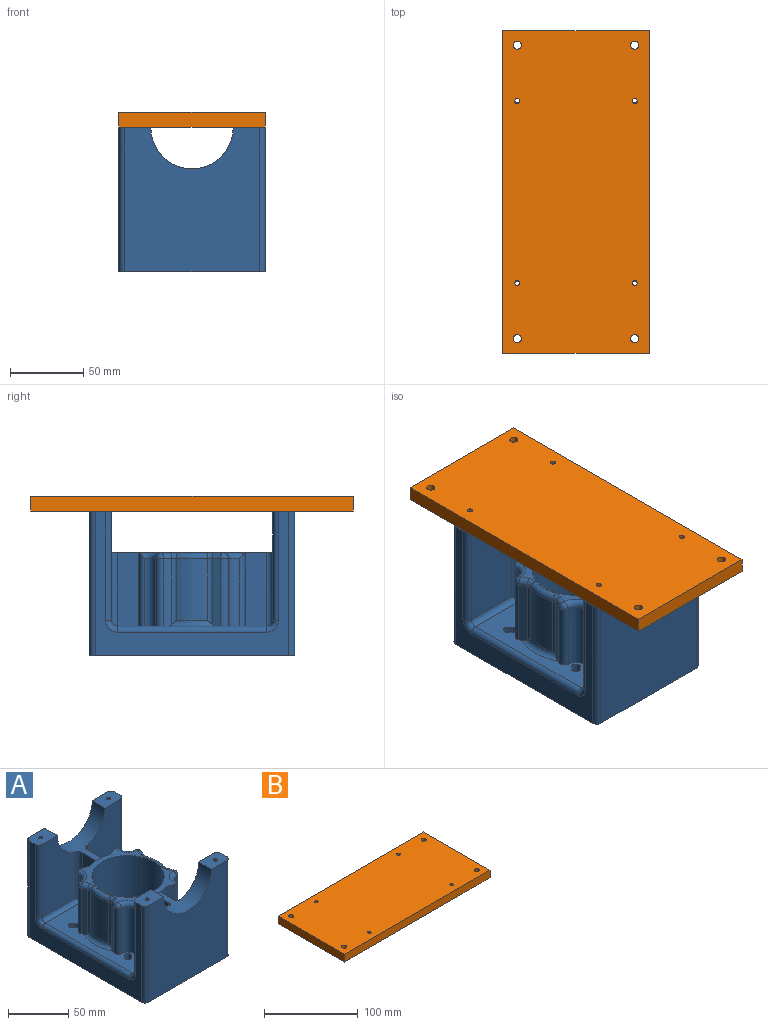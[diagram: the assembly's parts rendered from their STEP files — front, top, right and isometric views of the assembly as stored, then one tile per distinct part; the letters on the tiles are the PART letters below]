
ASSEMBLY  parts=2 mates=1
PART A: 127 faces, bbox 100.1x140.1x98.1 mm
  f0: plane 22x15mm, normal (0,0,1), area 313.5mm2, adj f8,f18,f19,f55,f71,f114,f121
  f1: plane 22x15mm, normal (0,0,1), area 313.5mm2, adj f5,f19,f20,f60,f65,f115,f122
  f2: plane 3x0.16mm, normal (0,-1,0), area 0.2mm2, adj f11,f53,f121
  f3: plane 3x0.16mm, normal (0,1,0), area 0.2mm2, adj f11,f62,f122
  f4: plane 140x100mm, normal (0,0,-1), area 10860.6mm2, adj f17,f18,f19,f20,f35,f37,f38,f39
  f5: cylinder r=1.75mm len=8.75mm, axis (0,0,1), area 96.2mm2, adj f1,f125
  f6: cylinder r=1.75mm len=8.75mm, axis (0,0,1), area 96.2mm2, adj f10,f126
  f7: cylinder r=1.75mm len=8.75mm, axis (0,0,1), area 96.2mm2, adj f9,f123
  f8: cylinder r=1.75mm len=8.75mm, axis (0,0,1), area 96.2mm2, adj f0,f124
  f9: plane 22x15mm, normal (0,0,1), area 313.5mm2, adj f7,f17,f18,f54,f80,f113,f121
  f10: plane 22x15mm, normal (0,0,1), area 313.5mm2, adj f6,f17,f20,f61,f73,f116,f122
  f11: plane 72.28x64.28mm, normal (0,0,1), area 956.9mm2, adj f2,f3,f13,f14,f15,f21,f22,f28
  f12: plane 102x43mm, normal (0,0,1), area 2152.4mm2, adj f15,f21,f29,f30,f31,f33,f34,f36
  f13: cylinder r=35mm len=50mm, axis (0,0,-1), area 473.7mm2, adj f11,f16,f22,f62
  f14: cylinder r=35mm len=50mm, axis (0,0,-1), area 473.7mm2, adj f11,f16,f28,f53
  f15: cylinder r=35mm len=50mm, axis (0,0,-1), area 473.7mm2, adj f11,f12,f29,f56
  f16: plane 102x43mm, normal (0,0,1), area 2152.4mm2, adj f13,f14,f22,f23,f24,f26,f27,f28
  f17: plane 132x98mm, normal (1,0,0), area 3287.5mm2, adj f4,f9,f10,f73,f75,f77,f79,f80
  f18: plane 98x92mm, normal (0,1,0), area 7784.5mm2, adj f0,f4,f9,f113,f114,f121
  f19: plane 132x98mm, normal (-1,0,0), area 3287.5mm2, adj f0,f1,f4,f65,f67,f69,f70,f71
  f20: plane 98x92mm, normal (0,-1,0), area 7784.5mm2, adj f1,f4,f10,f115,f116,f122
  f21: cylinder r=35mm len=50mm, axis (0,0,-1), area 473.7mm2, adj f11,f12,f36,f59
  f22: plane 50x7.13mm, normal (-0.39,-0.92,0), area 387mm2, adj f11,f13,f16,f89
  f23: cylinder r=8mm len=46mm, axis (0,0,-1), area 532.7mm2, adj f16,f89,f92,f93
  f24: plane 46.09x5.79mm, normal (0.92,0.39,0), area 283.5mm2, adj f16,f88,f91,f92,f96
  f25: cylinder r=35mm len=42mm, axis (0,0,-1), area 925.3mm2, adj f86,f88,f90,f91
  f26: plane 46.09x5.79mm, normal (0.92,-0.39,0), area 283.5mm2, adj f16,f83,f85,f86,f88
  f27: cylinder r=8mm len=46mm, axis (0,0,-1), area 532.7mm2, adj f16,f81,f82,f83
  f28: plane 50x7.13mm, normal (-0.39,0.92,0), area 387mm2, adj f11,f14,f16,f81
  f29: plane 50x7.13mm, normal (0.39,0.92,0), area 387mm2, adj f11,f12,f15,f105
  f30: cylinder r=8mm len=46mm, axis (0,0,-1), area 532.7mm2, adj f12,f105,f108,f109
  f31: plane 46.09x5.79mm, normal (-0.92,-0.39,0), area 283.5mm2, adj f12,f104,f107,f108,f112
  f32: cylinder r=35mm len=42mm, axis (0,0,-1), area 925.3mm2, adj f102,f104,f106,f107
  f33: plane 46.09x5.79mm, normal (-0.92,0.39,0), area 283.5mm2, adj f12,f99,f101,f102,f104
  f34: cylinder r=8mm len=46mm, axis (0,0,-1), area 532.7mm2, adj f12,f97,f98,f99
  f35: cylinder r=30mm len=70mm, axis (0,0,-1), area 13194.7mm2, adj f4,f11
  f36: plane 50x7.13mm, normal (0.39,-0.92,0), area 387mm2, adj f11,f12,f21,f97
  f37: plane 20x2.12mm, normal (-0.71,-0.71,0), area 60mm2, adj f4,f12,f38,f40
  f38: cylinder r=3mm len=20mm, axis (0,0,1), area 188.5mm2, adj f4,f12,f37,f39
  f39: plane 20x2.12mm, normal (0.71,0.71,0), area 60mm2, adj f4,f12,f38,f40
  f40: cylinder r=3mm len=20mm, axis (0,0,1), area 188.5mm2, adj f4,f12,f37,f39
  f41: plane 20x2.12mm, normal (-0.71,0.71,0), area 60mm2, adj f4,f16,f42,f44
  f42: cylinder r=3mm len=20mm, axis (0,0,1), area 188.5mm2, adj f4,f16,f41,f43
  f43: plane 20x2.12mm, normal (0.71,-0.71,0), area 60mm2, adj f4,f16,f42,f44
  f44: cylinder r=3mm len=20mm, axis (0,0,1), area 188.5mm2, adj f4,f16,f41,f43
  f45: plane 20x2.12mm, normal (-0.71,-0.71,0), area 60mm2, adj f4,f16,f46,f48
  f46: cylinder r=3mm len=20mm, axis (0,0,1), area 188.5mm2, adj f4,f16,f45,f47
  f47: plane 20x2.12mm, normal (0.71,0.71,0), area 60mm2, adj f4,f16,f46,f48
  f48: cylinder r=3mm len=20mm, axis (0,0,1), area 188.5mm2, adj f4,f16,f45,f47
  f49: plane 20x2.12mm, normal (-0.71,0.71,0), area 60mm2, adj f4,f12,f50,f52
  f50: cylinder r=3mm len=20mm, axis (0,0,1), area 188.5mm2, adj f4,f12,f49,f51
  f51: plane 20x2.12mm, normal (0.71,-0.71,0), area 60mm2, adj f4,f12,f50,f52
  f52: cylinder r=3mm len=20mm, axis (0,0,1), area 188.5mm2, adj f4,f12,f49,f51
  f53: plane 50.16x16.13mm, normal (1,0,0), area 809mm2, adj f2,f14,f16,f76,f121
  f54: plane 74x39mm, normal (0,-1,0), area 2464.2mm2, adj f9,f76,f78,f80,f121
  f55: plane 74x39mm, normal (0,-1,0), area 2464.2mm2, adj f0,f66,f68,f71,f121
  f56: plane 50.16x16.13mm, normal (-1,0,0), area 809mm2, adj f12,f15,f57,f66,f121
  f57: plane 3x0.16mm, normal (0,-1,0), area 0.2mm2, adj f11,f56,f121
  f58: plane 3x0.16mm, normal (0,1,0), area 0.2mm2, adj f11,f59,f122
  f59: plane 50.16x16.13mm, normal (-1,0,0), area 809mm2, adj f12,f21,f58,f63,f122
  f60: plane 74x39mm, normal (0,1,0), area 2464.2mm2, adj f1,f63,f64,f65,f122
  f61: plane 74x39mm, normal (0,1,0), area 2464.2mm2, adj f10,f72,f73,f74,f122
  f62: plane 50.16x16.13mm, normal (1,0,0), area 809mm2, adj f3,f13,f16,f72,f122
  f63: cylinder r=4mm len=50.89mm, axis (0,0,1), area 307.4mm2, adj f59,f60,f64,f122
  f64: cylinder r=4mm len=43mm, axis (-1,0,0), area 261mm2, adj f12,f60,f63,f67
  f65: cylinder r=4mm len=74mm, axis (0,0,1), area 465mm2, adj f1,f19,f60,f67
  f66: cylinder r=4mm len=50.89mm, axis (0,0,1), area 307.4mm2, adj f55,f56,f68,f121
  f67: torus R=8mm, axis (1,0,0), area 53.8mm2, adj f19,f64,f65,f69
  f68: cylinder r=4mm len=43mm, axis (1,0,0), area 261mm2, adj f12,f55,f66,f70
  f69: cylinder r=4mm len=102mm, axis (0,1,0), area 640.9mm2, adj f12,f19,f67,f70
  f70: torus R=8mm, axis (1,0,0), area 53.8mm2, adj f19,f68,f69,f71
  f71: cylinder r=4mm len=74mm, axis (0,0,-1), area 465mm2, adj f0,f19,f55,f70
  f72: cylinder r=4mm len=50.89mm, axis (0,0,-1), area 307.4mm2, adj f61,f62,f74,f122
  f73: cylinder r=4mm len=74mm, axis (0,0,-1), area 465mm2, adj f10,f17,f61,f75
  f74: cylinder r=4mm len=43mm, axis (-1,0,0), area 261mm2, adj f16,f61,f72,f75
  f75: torus R=8mm, axis (1,0,0), area 53.8mm2, adj f17,f73,f74,f77
  f76: cylinder r=4mm len=50.89mm, axis (0,0,-1), area 307.4mm2, adj f53,f54,f78,f121
  f77: cylinder r=4mm len=102mm, axis (0,-1,0), area 640.9mm2, adj f16,f17,f75,f79
  f78: cylinder r=4mm len=43mm, axis (1,0,0), area 261mm2, adj f16,f54,f76,f79
  f79: torus R=8mm, axis (1,0,0), area 53.8mm2, adj f17,f77,f78,f80
  f80: cylinder r=4mm len=74mm, axis (0,0,1), area 465mm2, adj f9,f17,f54,f79
  f81: cylinder r=4mm len=50mm, axis (0,0,-1), area 374.4mm2, adj f11,f16,f27,f28,f82
  f82: torus R=12mm, axis (0,0,1), area 100.6mm2, adj f11,f27,f81,f84
  f83: cylinder r=4mm len=46mm, axis (0,0,-1), area 351.6mm2, adj f16,f26,f27,f84
  f84: sphere r=4mm, area 30.6mm2, adj f82,f83,f85
  f85: cylinder r=4mm len=7.27mm, axis (-0.39,-0.92,0), area 38.9mm2, adj f11,f26,f84,f87
  f86: cylinder r=4mm len=44.73mm, axis (0,0,-1), area 124.4mm2, adj f25,f26,f87,f88
  f87: torus R=8mm, axis (0,0,1), area 24.5mm2, adj f11,f85,f86,f90
  f88: torus R=39mm, axis (0,0,1), area 179.2mm2, adj f16,f24,f25,f26,f86,f91
  f89: cylinder r=4mm len=50mm, axis (0,0,-1), area 374.4mm2, adj f11,f16,f22,f23,f93
  f90: torus R=31mm, axis (0,0,1), area 132.7mm2, adj f11,f25,f87,f94
  f91: cylinder r=4mm len=44.73mm, axis (0,0,-1), area 124.4mm2, adj f24,f25,f88,f94
  f92: cylinder r=4mm len=46mm, axis (0,0,-1), area 351.6mm2, adj f16,f23,f24,f95
  f93: torus R=12mm, axis (0,0,1), area 100.6mm2, adj f11,f23,f89,f95
  f94: torus R=8mm, axis (0,0,1), area 24.5mm2, adj f11,f90,f91,f96
  f95: sphere r=4mm, area 30.6mm2, adj f92,f93,f96
  f96: cylinder r=4mm len=7.27mm, axis (0.39,-0.92,0), area 38.9mm2, adj f11,f24,f94,f95
  f97: cylinder r=4mm len=50mm, axis (0,0,-1), area 374.4mm2, adj f11,f12,f34,f36,f98
  f98: torus R=12mm, axis (0,0,1), area 100.6mm2, adj f11,f34,f97,f100
  f99: cylinder r=4mm len=46mm, axis (0,0,-1), area 351.6mm2, adj f12,f33,f34,f100
  f100: sphere r=4mm, area 30.6mm2, adj f98,f99,f101
  f101: cylinder r=4mm len=7.27mm, axis (0.39,0.92,0), area 38.9mm2, adj f11,f33,f100,f103
  f102: cylinder r=4mm len=44.73mm, axis (0,0,-1), area 124.4mm2, adj f32,f33,f103,f104
  f103: torus R=8mm, axis (0,0,1), area 24.5mm2, adj f11,f101,f102,f106
  f104: torus R=39mm, axis (0,0,1), area 179.2mm2, adj f12,f31,f32,f33,f102,f107
  f105: cylinder r=4mm len=50mm, axis (0,0,-1), area 374.4mm2, adj f11,f12,f29,f30,f109
  f106: torus R=31mm, axis (0,0,1), area 132.7mm2, adj f11,f32,f103,f110
  f107: cylinder r=4mm len=44.73mm, axis (0,0,-1), area 124.4mm2, adj f31,f32,f104,f110
  f108: cylinder r=4mm len=46mm, axis (0,0,-1), area 351.6mm2, adj f12,f30,f31,f111
  f109: torus R=12mm, axis (0,0,1), area 100.6mm2, adj f11,f30,f105,f111
  f110: torus R=8mm, axis (0,0,1), area 24.5mm2, adj f11,f106,f107,f112
  f111: sphere r=4mm, area 30.6mm2, adj f108,f109,f112
  f112: cylinder r=4mm len=7.27mm, axis (-0.39,0.92,0), area 38.9mm2, adj f11,f31,f110,f111
  f113: cylinder r=4mm len=98mm, axis (0,0,1), area 615.8mm2, adj f4,f9,f17,f18
  f114: cylinder r=4mm len=98mm, axis (0,0,-1), area 615.8mm2, adj f0,f4,f18,f19
  f115: cylinder r=4mm len=98mm, axis (0,0,1), area 615.8mm2, adj f1,f4,f19,f20
  f116: cylinder r=4mm len=98mm, axis (0,0,-1), area 615.8mm2, adj f4,f10,f17,f20
  f117: cylinder r=3mm len=88mm, axis (0,0,-1), area 1658.8mm2, adj f4,f124
  f118: cylinder r=3mm len=88mm, axis (0,0,-1), area 1658.8mm2, adj f4,f123
  f119: cylinder r=3mm len=88mm, axis (0,0,-1), area 1658.8mm2, adj f4,f126
  f120: cylinder r=3mm len=88mm, axis (0,0,-1), area 1658.8mm2, adj f4,f125
  f121: cylinder r=28mm len=56mm, axis (0,-1,0), area 1447.4mm2, adj f0,f2,f9,f18,f53,f54,f55,f56
  f122: cylinder r=28mm len=56mm, axis (0,-1,0), area 1447.4mm2, adj f1,f3,f10,f20,f58,f59,f60,f61
  f123: cone r=1mm half-angle=45deg, axis (0,0,-1), area 26.4mm2, adj f7,f118
  f124: cone r=3mm half-angle=45deg, axis (0,0,-1), area 26.4mm2, adj f8,f117
  f125: cone r=1mm half-angle=45deg, axis (0,0,-1), area 26.4mm2, adj f5,f120
  f126: cone r=3mm half-angle=45deg, axis (0,0,-1), area 26.4mm2, adj f6,f119
PART B: 14 faces, bbox 220x100x10 mm
  f0: plane 100x10mm, normal (1,0,0), area 1000mm2, adj f1,f10,f12,f13
  f1: plane 220x10mm, normal (0,1,0), area 2200mm2, adj f0,f2,f12,f13
  f2: plane 100x10mm, normal (-1,0,0), area 1000mm2, adj f1,f10,f12,f13
  f3: cylinder r=1.75mm len=10mm, axis (0,0,-1), area 110mm2, adj f12,f13
  f4: cylinder r=1.75mm len=10mm, axis (0,0,-1), area 110mm2, adj f12,f13
  f5: cylinder r=1.75mm len=10mm, axis (0,0,-1), area 110mm2, adj f12,f13
  f6: cylinder r=1.75mm len=10mm, axis (0,0,-1), area 110mm2, adj f12,f13
  f7: cylinder r=2.75mm len=10mm, axis (0,0,-1), area 172.8mm2, adj f12,f13
  f8: cylinder r=2.75mm len=10mm, axis (0,0,-1), area 172.8mm2, adj f12,f13
  f9: cylinder r=2.75mm len=10mm, axis (0,0,-1), area 172.8mm2, adj f12,f13
  f10: plane 220x10mm, normal (0,-1,0), area 2200mm2, adj f0,f2,f12,f13
  f11: cylinder r=2.75mm len=10mm, axis (0,0,-1), area 172.8mm2, adj f12,f13
  f12: plane 220x100mm, normal (0,0,1), area 21866.5mm2, adj f0,f1,f2,f3,f4,f5,f6,f7
  f13: plane 220x100mm, normal (0,0,-1), area 21866.5mm2, adj f0,f1,f2,f3,f4,f5,f6,f7
PLACE A t=(-4.8,-23.71,13.39)mm
PLACE B rot(axis=(0,0,1),90deg) t=(-4.8,-23.71,111.99)mm
MATE slider A.f35 <-> B.f13  axis (0,0,-1) through (-4.8,-23.71,83.39)mm
